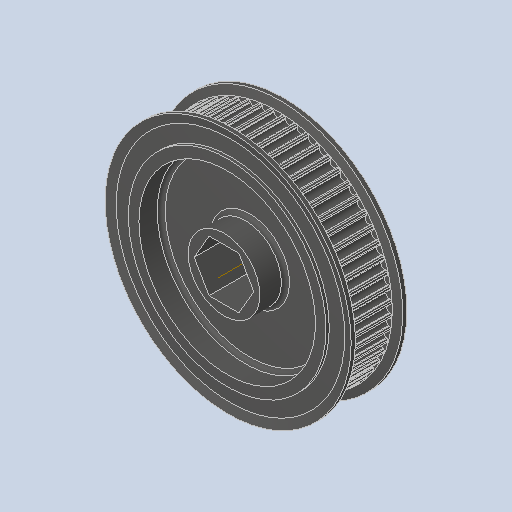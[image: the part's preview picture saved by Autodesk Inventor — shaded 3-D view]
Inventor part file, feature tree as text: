
AUTODESK INVENTOR PART (.ipt)
format: ipt  version: 2023.4 (Build 274418000, 418)  size: 570,880 bytes
history: native  units: in
note: dims shown in document units (in); Inventor stores cm internally (conversion verified against a paired STEP export)
features: plane x1, fillet x1
ambient origin geometry x8: Origin, YZ Plane, XZ Plane, XY Plane, X Axis, Y Axis, Z Axis, Center Point
bodies: Solid1 (feature_tree)
feature tree (2):
  plane  "Work Plane1"
  fillet  "Fillet1"  [1 undecoded]
note: 1 required parameter value undecoded (feature->parameter linkage not recoverable at this tier; creation-order binding heuristic only, values carry confidence <= 0.55)
